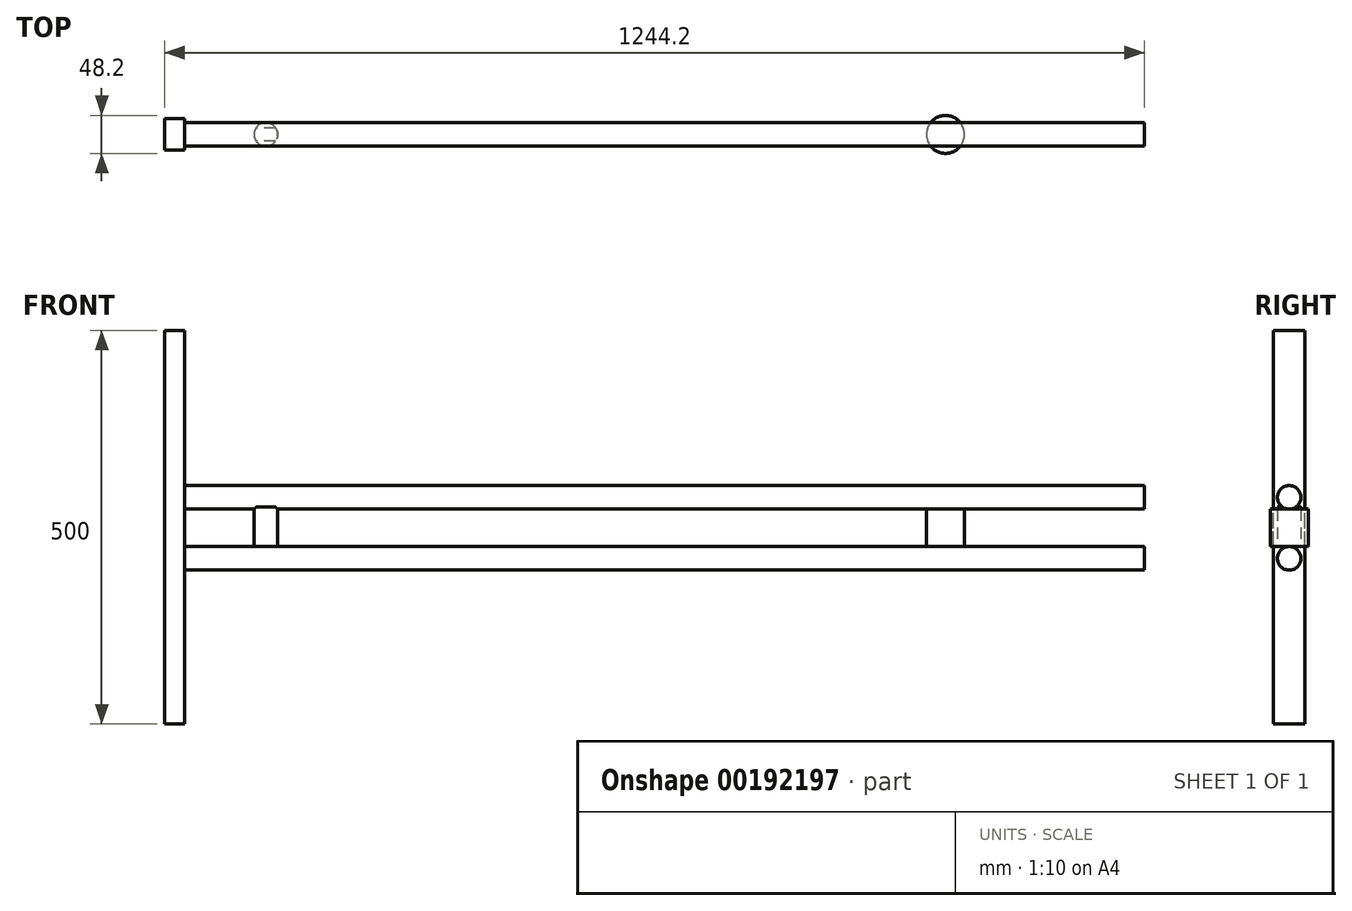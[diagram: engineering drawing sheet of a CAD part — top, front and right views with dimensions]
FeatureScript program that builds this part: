
annotation { "Feature Type Name" : "Feature", "Feature Type Description" : "" }
export const myFeature = defineFeature(function(context is Context, id is Id, definition is map)
    precondition{}
    {
        {
            var Q0;
            Q0=qCreatedBy(makeId("Front.planeOp"),FACE);
            var sketch = newSketch(context, id + "F0", { "sketchPlane" : qUnion([Q0])});
            skLineSegment(sketch, "E0.bottom", {"start": v(764.2, -22.5) * mm, "end": v(-454.93, -22.5) * mm});
            skLineSegment(sketch, "E0.top", {"start": v(764.2, 7.5) * mm, "end": v(-454.93, 7.5) * mm});
            skLineSegment(sketch, "E0.left", {"start": v(764.2, -22.5) * mm, "end": v(764.2, 7.5) * mm});
            skLineSegment(sketch, "E0.right", {"start": v(-454.93, -22.5) * mm, "end": v(-454.93, 7.5) * mm});
            skLineSegment(sketch, "E1.bottom", {"start": v(-336.59, 7.5) * mm, "end": v(-366.59, 7.5) * mm});
            skLineSegment(sketch, "E1.top", {"start": v(-336.59, 57.5) * mm, "end": v(-366.59, 57.5) * mm});
            skLineSegment(sketch, "E1.left", {"start": v(-336.59, 7.5) * mm, "end": v(-336.59, 57.5) * mm});
            skLineSegment(sketch, "E1.right", {"start": v(-366.59, 7.5) * mm, "end": v(-366.59, 57.5) * mm});
            skPoint(sketch, "E2.startSnap0", {"position": v(-366.59, 32.5) * mm});
            skPoint(sketch, "E2.endSnap0", {"position": v(-336.59, 32.5) * mm});
            skLineSegment(sketch, "E3", {"start": v(487.63, 32.5) * mm, "end": v(535.83, 32.5) * mm});
            skLineSegment(sketch, "E4.bottom", {"start": v(535.83, 7.5) * mm, "end": v(487.63, 7.5) * mm});
            skLineSegment(sketch, "E4.top", {"start": v(535.83, 57.5) * mm, "end": v(487.63, 57.5) * mm});
            skLineSegment(sketch, "E4.left", {"start": v(535.83, 7.5) * mm, "end": v(535.83, 57.5) * mm});
            skLineSegment(sketch, "E4.right", {"start": v(487.63, 7.5) * mm, "end": v(487.63, 57.5) * mm});
            skPoint(sketch, "E4.middle", {"position": v(511.73, 32.5) * mm});
            skLineSegment(sketch, "E5", {"start": v(-454.93, -7.5) * mm, "end": v(764.2, -7.5) * mm});
            skLineSegment(sketch, "E6", {"start": v(-351.59, 7.5) * mm, "end": v(-351.59, 57.5) * mm});
            skLineSegment(sketch, "E7", {"start": v(511.73, 57.5) * mm, "end": v(511.73, 7.5) * mm});
            skLineSegment(sketch, "E8", {"start": v(-454.93, 55) * mm, "end": v(-454.93, 85) * mm});
            skLineSegment(sketch, "E9.bottom", {"start": v(-454.93, 55) * mm, "end": v(764.27, 55) * mm});
            skLineSegment(sketch, "E9.top", {"start": v(-454.93, 85) * mm, "end": v(764.27, 85) * mm});
            skLineSegment(sketch, "E9.right", {"start": v(764.27, 55) * mm, "end": v(764.27, 85) * mm});
            skPoint(sketch, "E9.middle", {"position": v(154.67, 70) * mm});
            skLineSegment(sketch, "E10", {"start": v(-454.93, 70) * mm, "end": v(764.27, 70) * mm});
            skSolve(sketch);
        }
        {
            var Q0;
            {var subQ0=sQuery(id+"F0.wireOp",EDGE,"E9.top");Q0=makeQuery(id+"F0.imprint","IMPRINT",FACE,{"disambiguationData":[TD([[makeQuery(id+"F0.imprint","IMPRINT",EDGE,{"derivedFrom":subQ0}),-1.0]])]});}
            var Q1;
            Q1=sQuery(id+"F0.wireOp",EDGE,"E10");
            revolve(context, id + "F1", {"entities" : qUnion([Q0]), "axis" : qUnion([Q1]), "revolveType" : RevolveType.FULL});
        }
        {
            var Q0;
            {var subQ3=sQuery(id+"F0.wireOp",EDGE,"E5");Q0=makeQuery(id+"F0.imprint","IMPRINT",FACE,{"disambiguationData":[TD([[makeQuery(id+"F0.imprint","IMPRINT",EDGE,{"derivedFrom":subQ3}),1.0]])]});}
            var Q1;
            Q1=sQuery(id+"F0.wireOp",EDGE,"E5");
            revolve(context, id + "F2", {"entities" : qUnion([Q0]), "axis" : qUnion([Q1]), "revolveType" : RevolveType.FULL});
        }
        {
            var Q0;
            {var subQ0=sQuery(id+"F0.wireOp",EDGE,"E1.right");Q0=makeQuery(id+"F0.imprint","IMPRINT",FACE,{"disambiguationData":[TD([[makeQuery(id+"F0.imprint","IMPRINT",EDGE,{"derivedFrom":subQ0}),-1.0]])]});}
            var Q1;
            Q1=sQuery(id+"F0.wireOp",EDGE,"E6");
            revolve(context, id + "F3", {"operationType" : NewBodyOperationType.ADD, "entities" : qUnion([Q0]), "axis" : qUnion([Q1]), "revolveType" : RevolveType.FULL});
        }
        {
            var Q0;
            {var subQ0=sQuery(id+"F0.wireOp",EDGE,"E4.right");var subQ1=sQuery(id+"F0.wireOp",EDGE,"E3");var subQ2=makeQuery(id+"F0.imprint","INTERSECT",VERTEX,{"derivedFrom":[subQ1,subQ0]});Q0=makeQuery(id+"F0.imprint","IMPRINT",FACE,{"disambiguationData":[TD([[makeQuery(id+"F0.imprint","IMPRINT",EDGE,{"disambiguationData":[TD([[subQ2,-1.0]])],"derivedFrom":subQ1}),1.0]])]});}
            var Q1;
            {var subQ0=sQuery(id+"F0.wireOp",EDGE,"E4.right");var subQ1=sQuery(id+"F0.wireOp",EDGE,"E3");var subQ2=makeQuery(id+"F0.imprint","INTERSECT",VERTEX,{"derivedFrom":[subQ1,subQ0]});Q1=makeQuery(id+"F0.imprint","IMPRINT",FACE,{"disambiguationData":[TD([[makeQuery(id+"F0.imprint","IMPRINT",EDGE,{"disambiguationData":[TD([[subQ2,-1.0]])],"derivedFrom":subQ1}),-1.0]])]});}
            var Q2;
            Q2=sQuery(id+"F0.wireOp",EDGE,"E7");
            revolve(context, id + "F4", {"operationType" : NewBodyOperationType.ADD, "entities" : qUnion([Q0, Q1]), "axis" : qUnion([Q2]), "revolveType" : RevolveType.FULL});
        }
        {
            var Q0;
            Q0=makeQuery(id+"F3.opRevolve","SWEPT_EDGE",EDGE,{"disambiguationData":[OSD([sQuery(id+"F0.wireOp",EDGE,"E1.top"),sQuery(id+"F0.wireOp",EDGE,"E1.right")])]});
            fillet(context, id + "F5", {"entities" : qUnion([Q0]), "radius" : 0.02 * mm, "tangentPropagation" : true, "allowEdgeOverflow" : false});
        }
        {
            var Q0;
            Q0=makeQuery(id+"F2.opRevolve","SWEPT_FACE",FACE,{"disambiguationData":[OSD([sQuery(id+"F0.wireOp",EDGE,"E0.right")])]});
            var sketch = newSketch(context, id + "F6", { "sketchPlane" : qUnion([Q0])});
            skLineSegment(sketch, "E11.bottom", {"start": v(-20, -218) * mm, "end": v(20, -218) * mm});
            skLineSegment(sketch, "E11.top", {"start": v(-20, 282) * mm, "end": v(20, 282) * mm});
            skLineSegment(sketch, "E11.left", {"start": v(-20, -218) * mm, "end": v(-20, 282) * mm});
            skLineSegment(sketch, "E11.right", {"start": v(20, -218) * mm, "end": v(20, 282) * mm});
            skPoint(sketch, "E11.middle", {"position": v(0, 32) * mm});
            skPoint(sketch, "E12.orphan", {"position": v(0, 282) * mm});
            skPoint(sketch, "E13.end.orphan", {"position": v(0, -218) * mm});
            skSolve(sketch);
        }
        {
            var Q0;
            Q0 = qSketchRegion(id + "F6", true);
            extrude(context, id + "F7", {"entities" : qUnion([Q0]), "depth" : 25 * mm});
        }
    });
